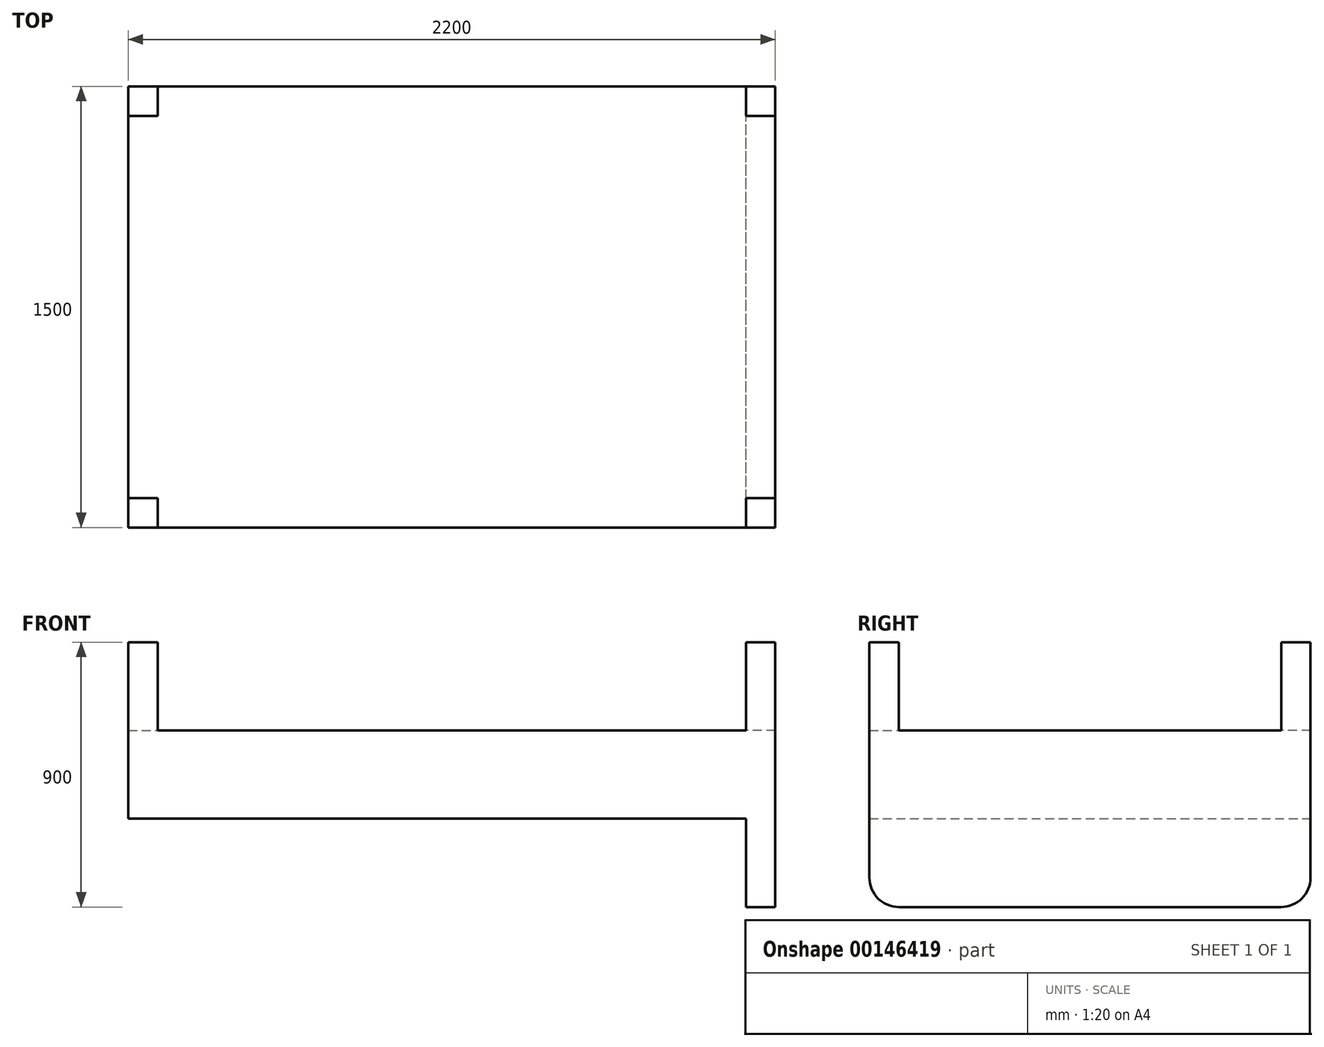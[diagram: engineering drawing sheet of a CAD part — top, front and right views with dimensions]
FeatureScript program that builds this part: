
annotation { "Feature Type Name" : "Feature", "Feature Type Description" : "" }
export const myFeature = defineFeature(function(context is Context, id is Id, definition is map)
    precondition{}
    {
        {
            var Q0;
            Q0=qCreatedBy(makeId("Top.planeOp"),FACE);
            var sketch = newSketch(context, id + "F0", { "sketchPlane" : qUnion([Q0])});
            skLineSegment(sketch, "E0.bottom", {"start": v(1100, -750) * mm, "end": v(-1100, -750) * mm});
            skLineSegment(sketch, "E0.top", {"start": v(1100, 750) * mm, "end": v(-1100, 750) * mm});
            skLineSegment(sketch, "E0.left", {"start": v(1100, -750) * mm, "end": v(1100, 750) * mm});
            skLineSegment(sketch, "E0.right", {"start": v(-1100, -750) * mm, "end": v(-1100, 750) * mm});
            skPoint(sketch, "E0.middle", {"position": v(0, 0) * mm});
            skSolve(sketch);
        }
        {
            var Q0;
            Q0=makeQuery(id+"F0.imprint","IMPRINT",FACE,{"disambiguationData":[TD([[makeQuery(id+"F0.imprint","IMPRINT",EDGE,{"derivedFrom":sQuery(id+"F0.wireOp",EDGE,"E0.bottom")}),-1.0]])]});
            extrude(context, id + "F1", {"entities" : qUnion([Q0]), "depth" : 300 * mm});
        }
        {
            var Q0;
            Q0=makeQuery(id+"F1.opExtrude","CAP_FACE",FACE,{"disambiguationData":[OSD([sQuery(id+"F0.wireOp",EDGE,"E0.bottom"),sQuery(id+"F0.wireOp",EDGE,"E0.top"),sQuery(id+"F0.wireOp",EDGE,"E0.left"),sQuery(id+"F0.wireOp",EDGE,"E0.right")])],"isStart":false});
            var sketch = newSketch(context, id + "F2", { "sketchPlane" : qUnion([Q0])});
            skLineSegment(sketch, "E1.bottom", {"start": v(-1100, -750) * mm, "end": v(-1000, -750) * mm});
            skLineSegment(sketch, "E1.top", {"start": v(-1100, -650) * mm, "end": v(-1000, -650) * mm});
            skLineSegment(sketch, "E1.left", {"start": v(-1100, -750) * mm, "end": v(-1100, -650) * mm});
            skLineSegment(sketch, "E1.right", {"start": v(-1000, -750) * mm, "end": v(-1000, -650) * mm});
            skLineSegment(sketch, "E2.bottom", {"start": v(-1100, 750) * mm, "end": v(-1000, 750) * mm});
            skLineSegment(sketch, "E2.top", {"start": v(-1100, 650) * mm, "end": v(-1000, 650) * mm});
            skLineSegment(sketch, "E2.left", {"start": v(-1100, 750) * mm, "end": v(-1100, 650) * mm});
            skLineSegment(sketch, "E2.right", {"start": v(-1000, 750) * mm, "end": v(-1000, 650) * mm});
            skLineSegment(sketch, "E3.bottom", {"start": v(1100, -750) * mm, "end": v(1000, -750) * mm});
            skLineSegment(sketch, "E3.top", {"start": v(1100, -650) * mm, "end": v(1000, -650) * mm});
            skLineSegment(sketch, "E3.left", {"start": v(1100, -750) * mm, "end": v(1100, -650) * mm});
            skLineSegment(sketch, "E3.right", {"start": v(1000, -750) * mm, "end": v(1000, -650) * mm});
            skLineSegment(sketch, "E4.bottom", {"start": v(1100, 750) * mm, "end": v(1000, 750) * mm});
            skLineSegment(sketch, "E4.top", {"start": v(1100, 650) * mm, "end": v(1000, 650) * mm});
            skLineSegment(sketch, "E4.left", {"start": v(1100, 750) * mm, "end": v(1100, 650) * mm});
            skLineSegment(sketch, "E4.right", {"start": v(1000, 750) * mm, "end": v(1000, 650) * mm});
            skSolve(sketch);
        }
        {
            var Q0;
            Q0 = qSketchRegion(id + "F2", true);
            extrude(context, id + "F3", {"entities" : qUnion([Q0]), "operationType" : NewBodyOperationType.ADD, "depth" : 300 * mm});
        }
        {
            var Q0;
            Q0=makeQuery(id+"F1.opExtrude","CAP_FACE",FACE,{"disambiguationData":[OSD([sQuery(id+"F0.wireOp",EDGE,"E0.bottom"),sQuery(id+"F0.wireOp",EDGE,"E0.top"),sQuery(id+"F0.wireOp",EDGE,"E0.left"),sQuery(id+"F0.wireOp",EDGE,"E0.right")])],"isStart":true});
            var sketch = newSketch(context, id + "F4", { "sketchPlane" : qUnion([Q0])});
            skLineSegment(sketch, "E5.bottom", {"start": v(1100, 750) * mm, "end": v(1000, 750) * mm});
            skLineSegment(sketch, "E5.top", {"start": v(1100, -750) * mm, "end": v(1000, -750) * mm});
            skLineSegment(sketch, "E5.left", {"start": v(1100, 750) * mm, "end": v(1100, -750) * mm});
            skLineSegment(sketch, "E5.right", {"start": v(1000, 750) * mm, "end": v(1000, -750) * mm});
            skSolve(sketch);
        }
        {
            var Q0;
            Q0 = qSketchRegion(id + "F4", true);
            extrude(context, id + "F5", {"entities" : qUnion([Q0]), "operationType" : NewBodyOperationType.ADD, "depth" : 300 * mm});
        }
        {
            var Q0;
            Q0=makeQuery(id+"F5.opExtrude","CAP_EDGE",EDGE,{"disambiguationData":[OSD([sQuery(id+"F4.wireOp",EDGE,"E5.bottom")])],"isStart":false});
            var Q1;
            Q1=makeQuery(id+"F5.opExtrude","CAP_EDGE",EDGE,{"disambiguationData":[OSD([sQuery(id+"F4.wireOp",EDGE,"E5.top")])],"isStart":false});
            fillet(context, id + "F6", {"entities" : qUnion([Q0, Q1]), "radius" : 100 * mm, "tangentPropagation" : true, "allowEdgeOverflow" : false});
        }
    });
